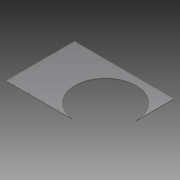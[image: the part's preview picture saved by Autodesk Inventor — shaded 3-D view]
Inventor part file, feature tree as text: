
AUTODESK INVENTOR PART (.ipt)
format: ipt  version: 2014 SP1 (Build 180222100, 222)  size: 104,448 bytes
history: native  units: in
note: dims shown in document units (in); Inventor stores cm internally (conversion verified against a paired STEP export)
features: reference x3, extrude x2, sketch x2, plane x1
ambient origin geometry x8: Origin, YZ Plane, XZ Plane, XY Plane, X Axis, Y Axis, Z Axis, Center Point
bodies: Solid1 (feature_tree)
feature tree (8):
  extrude  "Extrusion1"  Depth=12.875in
  plane  "Work Plane1"
  extrude  "Extrusion2"  Depth=5.75in
  sketch  "Sketch1"  dims[d0=12.875in d1=13.0in]
  reference  "Reference1"
  sketch  "Sketch2"  dims[d2=18.75in d3=5.75in d4=7.125in d5=0.125in d6=0.0in d7=1.0in d8=0.0in d9=0.04in]
  reference  "Reference2"
  reference  "Reference3"
